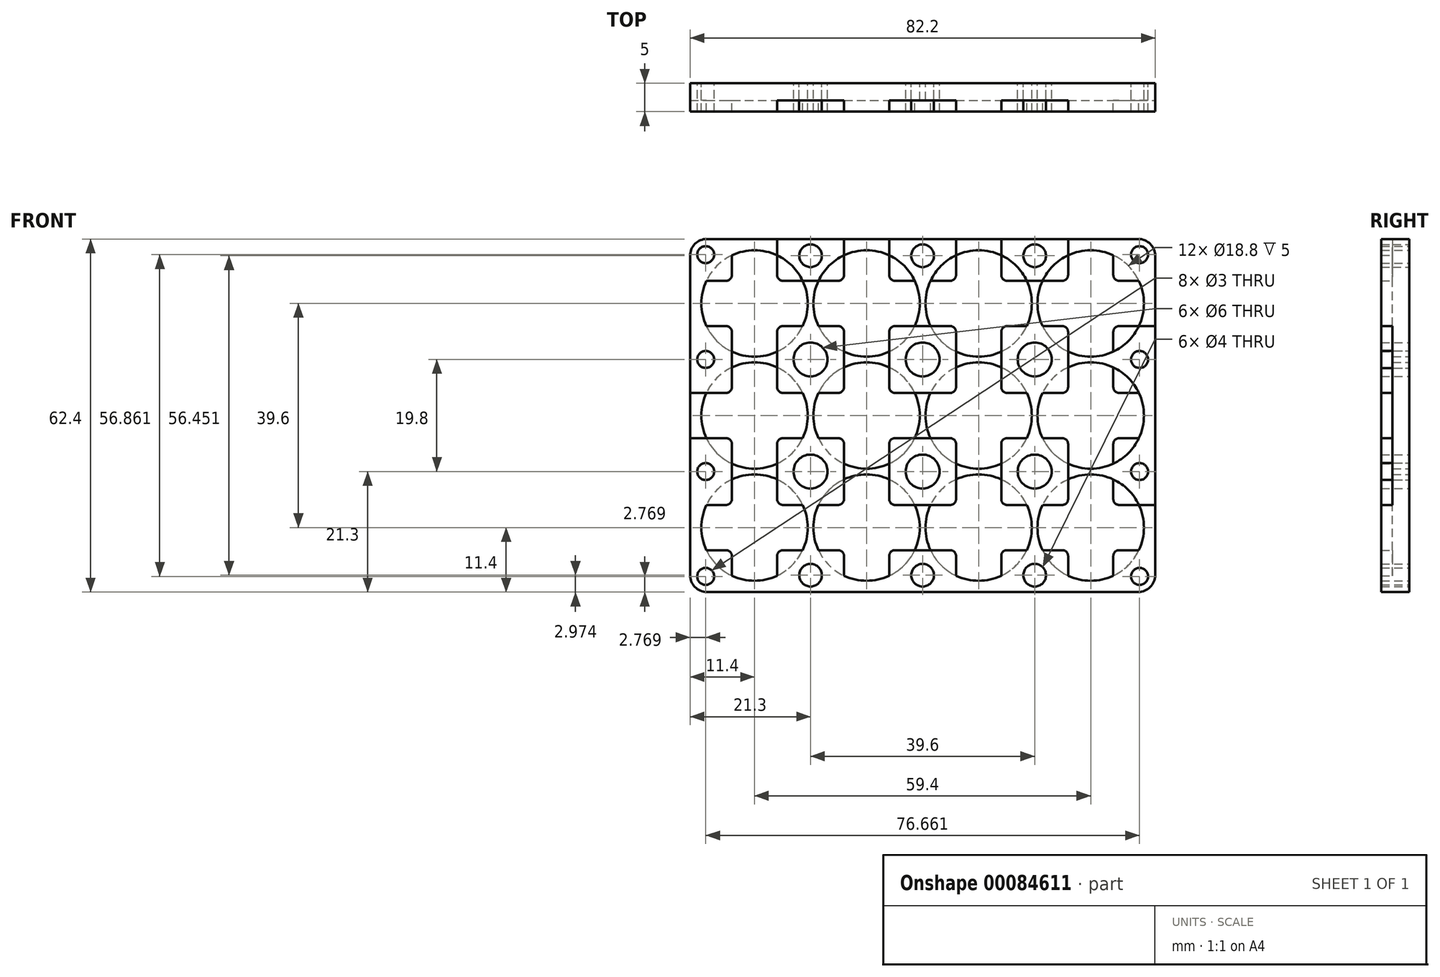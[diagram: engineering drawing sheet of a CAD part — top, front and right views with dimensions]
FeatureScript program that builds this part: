
annotation { "Feature Type Name" : "Feature", "Feature Type Description" : "" }
export const myFeature = defineFeature(function(context is Context, id is Id, definition is map)
    precondition{}
    {
        {
            var Q0;
            Q0=qCreatedBy(makeId("Front.planeOp"),FACE);
            var sketch = newSketch(context, id + "F0", { "sketchPlane" : qUnion([Q0]) });
            skCircle(sketch, "E0", {"center": v(0, 0) * mm, "radius": 9.4 * mm});
            skCircle(sketch, "E1.0.1.0", {"center": v(0, 19.8) * mm, "radius": 9.4 * mm});
            skCircle(sketch, "E1.0.2.0", {"center": v(0, 39.6) * mm, "radius": 9.4 * mm});
            skCircle(sketch, "E1.1.0.0", {"center": v(19.8, 0) * mm, "radius": 9.4 * mm});
            skCircle(sketch, "E1.1.1.0", {"center": v(19.8, 19.8) * mm, "radius": 9.4 * mm});
            skCircle(sketch, "E1.1.2.0", {"center": v(19.8, 39.6) * mm, "radius": 9.4 * mm});
            skCircle(sketch, "E1.2.0.0", {"center": v(39.6, 0) * mm, "radius": 9.4 * mm});
            skCircle(sketch, "E1.2.1.0", {"center": v(39.6, 19.8) * mm, "radius": 9.4 * mm});
            skCircle(sketch, "E1.2.2.0", {"center": v(39.6, 39.6) * mm, "radius": 9.4 * mm});
            skCircle(sketch, "E1.3.0.0", {"center": v(59.4, 0) * mm, "radius": 9.4 * mm});
            skCircle(sketch, "E1.3.1.0", {"center": v(59.4, 19.8) * mm, "radius": 9.4 * mm});
            skCircle(sketch, "E1.3.2.0", {"center": v(59.4, 39.6) * mm, "radius": 9.4 * mm});
            skLineSegment(sketch, "E1.direction1", {"start": v(0, 0) * mm, "end": v(19.8, 0) * mm, "construction": true});
            skLineSegment(sketch, "E1.direction2", {"start": v(0, 0) * mm, "end": v(0, 19.8) * mm, "construction": true});
            skLineSegment(sketch, "E2", {"start": v(-9.4, 19.8) * mm, "end": v(68.8, 19.8) * mm, "construction": true});
            skLineSegment(sketch, "E3", {"start": v(29.7, 19.8) * mm, "end": v(29.7, -16.3) * mm, "construction": true});
            skLineSegment(sketch, "E4.bottom", {"start": v(70.8, -11.4) * mm, "end": v(-11.4, -11.4) * mm});
            skLineSegment(sketch, "E4.top", {"start": v(70.8, 51) * mm, "end": v(-11.4, 51) * mm});
            skLineSegment(sketch, "E4.left", {"start": v(70.8, -11.4) * mm, "end": v(70.8, 51) * mm});
            skLineSegment(sketch, "E4.right", {"start": v(-11.4, -11.4) * mm, "end": v(-11.4, 51) * mm});
            skPoint(sketch, "E4.middle", {"position": v(29.7, 19.8) * mm});
            skLineSegment(sketch, "E5", {"start": v(19.8, 19.8) * mm, "end": v(0, 0) * mm, "construction": true});
            skLineSegment(sketch, "E6", {"start": v(19.8, 0) * mm, "end": v(0, 19.8) * mm, "construction": true});
            skCircle(sketch, "E7", {"center": v(9.9, 9.9) * mm, "radius": 3 * mm});
            skCircle(sketch, "E8.0.1.0", {"center": v(9.9, 29.7) * mm, "radius": 3 * mm});
            skCircle(sketch, "E8.1.0.0", {"center": v(29.7, 9.9) * mm, "radius": 3 * mm});
            skCircle(sketch, "E8.1.1.0", {"center": v(29.7, 29.7) * mm, "radius": 3 * mm});
            skCircle(sketch, "E8.2.0.0", {"center": v(49.5, 9.9) * mm, "radius": 3 * mm});
            skCircle(sketch, "E8.2.1.0", {"center": v(49.5, 29.7) * mm, "radius": 3 * mm});
            skLineSegment(sketch, "E8.direction1", {"start": v(9.9, 9.9) * mm, "end": v(29.7, 9.9) * mm, "construction": true});
            skLineSegment(sketch, "E8.direction2", {"start": v(9.9, 9.9) * mm, "end": v(9.9, 29.7) * mm, "construction": true});
            skLineSegment(sketch, "E9", {"start": v(9.9, 0) * mm, "end": v(9.9, -11.4) * mm, "construction": true});
            skCircle(sketch, "E10", {"center": v(9.9, -8.43) * mm, "radius": 2 * mm});
            skCircle(sketch, "E11.1.0.0", {"center": v(29.7, -8.43) * mm, "radius": 2 * mm});
            skCircle(sketch, "E11.2.0.0", {"center": v(49.5, -8.43) * mm, "radius": 2 * mm});
            skLineSegment(sketch, "E11.direction1", {"start": v(9.9, -8.43) * mm, "end": v(29.7, -8.43) * mm, "construction": true});
            skCircle(sketch, "E12.MirrorC", {"center": v(9.9, 48.03) * mm, "radius": 2 * mm});
            skCircle(sketch, "E13.MirrorC", {"center": v(29.7, 48.03) * mm, "radius": 2 * mm});
            skCircle(sketch, "E14.MirrorC", {"center": v(49.5, 48.03) * mm, "radius": 2 * mm});
            skLineSegment(sketch, "E15", {"start": v(0, 0) * mm, "end": v(-11.4, -11.4) * mm, "construction": true});
            skCircle(sketch, "E16", {"center": v(-8.63, -8.63) * mm, "radius": 1.5 * mm});
            skCircle(sketch, "E17", {"center": v(-8.63, 9.9) * mm, "radius": 1.5 * mm});
            skCircle(sketch, "E18", {"center": v(-8.63, 29.7) * mm, "radius": 1.5 * mm});
            skCircle(sketch, "E19.MirrorC", {"center": v(-8.63, 48.23) * mm, "radius": 1.5 * mm});
            skCircle(sketch, "E20.MirrorC", {"center": v(68.03, -8.63) * mm, "radius": 1.5 * mm});
            skCircle(sketch, "E21.MirrorC", {"center": v(68.03, 9.9) * mm, "radius": 1.5 * mm});
            skCircle(sketch, "E22.MirrorC", {"center": v(68.03, 29.7) * mm, "radius": 1.5 * mm});
            skCircle(sketch, "E23.MirrorC", {"center": v(68.03, 48.23) * mm, "radius": 1.5 * mm});
            skSolve(sketch);
        }
        {
            var Q0;
            Q0=qSketchRegion(id+"F0",true);
            extrude(context, id + "F1", {"entities" : qUnion([Q0]), "depth" : 3 * mm});
        }
        {
            var Q0;
            Q0=makeQuery(id+"F1.opExtrude","SWEPT_EDGE",EDGE,{"disambiguationData":[OSD([sQuery(id+"F0.wireOp",EDGE,"E4.top"),sQuery(id+"F0.wireOp",EDGE,"E4.left")])]});
            var Q1;
            Q1=makeQuery(id+"F1.opExtrude","SWEPT_EDGE",EDGE,{"disambiguationData":[OSD([sQuery(id+"F0.wireOp",EDGE,"E4.top"),sQuery(id+"F0.wireOp",EDGE,"E4.right")])]});
            var Q2;
            Q2=makeQuery(id+"F1.opExtrude","SWEPT_EDGE",EDGE,{"disambiguationData":[OSD([sQuery(id+"F0.wireOp",EDGE,"E4.bottom"),sQuery(id+"F0.wireOp",EDGE,"E4.right")])]});
            var Q3;
            Q3=makeQuery(id+"F1.opExtrude","SWEPT_EDGE",EDGE,{"disambiguationData":[OSD([sQuery(id+"F0.wireOp",EDGE,"E4.bottom"),sQuery(id+"F0.wireOp",EDGE,"E4.left")])]});
            fillet(context, id + "F2", {"entities" : qUnion([Q0, Q1, Q2, Q3]), "radius" : 3 * mm, "tangentPropagation" : true, "conicFillet" : false});
        }
        {
            var Q0;
            Q0=makeQuery(id+"F1.opExtrude","CAP_FACE",FACE,{"disambiguationData":[OSD([sQuery(id+"F0.wireOp",EDGE,"E0"),sQuery(id+"F0.wireOp",EDGE,"E1.0.1.0"),sQuery(id+"F0.wireOp",EDGE,"E1.0.2.0"),sQuery(id+"F0.wireOp",EDGE,"E1.1.0.0"),sQuery(id+"F0.wireOp",EDGE,"E1.1.1.0"),sQuery(id+"F0.wireOp",EDGE,"E1.1.2.0"),sQuery(id+"F0.wireOp",EDGE,"E1.2.0.0"),sQuery(id+"F0.wireOp",EDGE,"E1.2.1.0"),sQuery(id+"F0.wireOp",EDGE,"E1.2.2.0"),sQuery(id+"F0.wireOp",EDGE,"E1.3.0.0"),sQuery(id+"F0.wireOp",EDGE,"E1.3.1.0"),sQuery(id+"F0.wireOp",EDGE,"E1.3.2.0"),sQuery(id+"F0.wireOp",EDGE,"E4.bottom"),sQuery(id+"F0.wireOp",EDGE,"E4.top"),sQuery(id+"F0.wireOp",EDGE,"E4.left"),sQuery(id+"F0.wireOp",EDGE,"E4.right"),sQuery(id+"F0.wireOp",EDGE,"E7"),sQuery(id+"F0.wireOp",EDGE,"E8.0.1.0"),sQuery(id+"F0.wireOp",EDGE,"E8.1.0.0"),sQuery(id+"F0.wireOp",EDGE,"E8.1.1.0"),sQuery(id+"F0.wireOp",EDGE,"E8.2.0.0"),sQuery(id+"F0.wireOp",EDGE,"E8.2.1.0"),sQuery(id+"F0.wireOp",EDGE,"E10"),sQuery(id+"F0.wireOp",EDGE,"E11.1.0.0"),sQuery(id+"F0.wireOp",EDGE,"E11.2.0.0"),sQuery(id+"F0.wireOp",EDGE,"E12.MirrorC"),sQuery(id+"F0.wireOp",EDGE,"E13.MirrorC"),sQuery(id+"F0.wireOp",EDGE,"E14.MirrorC"),sQuery(id+"F0.wireOp",EDGE,"E16"),sQuery(id+"F0.wireOp",EDGE,"E17"),sQuery(id+"F0.wireOp",EDGE,"E18"),sQuery(id+"F0.wireOp",EDGE,"E19.MirrorC"),sQuery(id+"F0.wireOp",EDGE,"E20.MirrorC"),sQuery(id+"F0.wireOp",EDGE,"E21.MirrorC"),sQuery(id+"F0.wireOp",EDGE,"E22.MirrorC"),sQuery(id+"F0.wireOp",EDGE,"E23.MirrorC")])],"isStart":false});
            var sketch = newSketch(context, id + "F3", { "sketchPlane" : qUnion([Q0]) });
            skLineSegment(sketch, "E24.0", {"start": v(67.8, 51) * mm, "end": v(-8.4, 51) * mm});
            skArc(sketch, "E24.1", {"start": v(-8.4, 51) * mm, "mid": v(-10.52, 50.12) * mm, "end": v(-11.4, 48) * mm});
            skLineSegment(sketch, "E24.2", {"start": v(-11.4, -8.4) * mm, "end": v(-11.4, 35.6) * mm});
            skArc(sketch, "E24.3", {"start": v(-11.4, -8.4) * mm, "mid": v(-10.52, -10.52) * mm, "end": v(-8.4, -11.4) * mm});
            skLineSegment(sketch, "E24.4", {"start": v(67.8, -11.4) * mm, "end": v(-8.4, -11.4) * mm});
            skArc(sketch, "E24.5", {"start": v(67.8, -11.4) * mm, "mid": v(69.92, -10.52) * mm, "end": v(70.8, -8.4) * mm});
            skLineSegment(sketch, "E24.6", {"start": v(70.8, -8.4) * mm, "end": v(70.8, 48) * mm});
            skArc(sketch, "E24.7", {"start": v(70.8, 48) * mm, "mid": v(69.92, 50.12) * mm, "end": v(67.8, 51) * mm});
            skCircle(sketch, "E24.8", {"center": v(59.4, 39.6) * mm, "radius": 9.4 * mm});
            skCircle(sketch, "E24.9", {"center": v(39.6, 39.6) * mm, "radius": 9.4 * mm});
            skCircle(sketch, "E24.10", {"center": v(19.8, 39.6) * mm, "radius": 9.4 * mm});
            skArc(sketch, "E24.11", {"start": v(-8.5, 43.6) * mm, "mid": v(-9.4, 39.6) * mm, "end": v(-8.5, 35.6) * mm});
            skCircle(sketch, "E24.12", {"center": v(0, 19.8) * mm, "radius": 9.4 * mm});
            skCircle(sketch, "E24.13", {"center": v(19.8, 19.8) * mm, "radius": 9.4 * mm});
            skCircle(sketch, "E24.14", {"center": v(39.6, 19.8) * mm, "radius": 9.4 * mm});
            skCircle(sketch, "E24.15", {"center": v(59.4, 19.8) * mm, "radius": 9.4 * mm});
            skCircle(sketch, "E24.16", {"center": v(59.4, 0) * mm, "radius": 9.4 * mm});
            skCircle(sketch, "E24.17", {"center": v(39.6, 0) * mm, "radius": 9.4 * mm});
            skCircle(sketch, "E24.18", {"center": v(19.8, 0) * mm, "radius": 9.4 * mm});
            skCircle(sketch, "E24.19", {"center": v(0, 0) * mm, "radius": 9.4 * mm});
            skLineSegment(sketch, "E25.left", {"start": v(-11.4, 39.6) * mm, "end": v(-11.4, 43.6) * mm});
            skLineSegment(sketch, "E25.right", {"start": v(70.8, 39.6) * mm, "end": v(70.8, 43.6) * mm});
            skLineSegment(sketch, "E26.trimOffspring", {"start": v(-11.4, 43.6) * mm, "end": v(-11.4, 48) * mm});
            skLineSegment(sketch, "E27", {"start": v(-4, 51) * mm, "end": v(-4, 43.6) * mm});
            skLineSegment(sketch, "E28.MirrorCS", {"start": v(4, 51) * mm, "end": v(4, 43.6) * mm});
            skLineSegment(sketch, "E29", {"start": v(-11.4, -4) * mm, "end": v(-4, -4) * mm});
            skLineSegment(sketch, "E30.MirrorCS", {"start": v(-11.4, 4) * mm, "end": v(-4, 4) * mm});
            skLineSegment(sketch, "E31.1.0.0", {"start": v(15.8, 51) * mm, "end": v(15.8, 43.6) * mm});
            skLineSegment(sketch, "E31.1.0.1", {"start": v(23.8, 51) * mm, "end": v(23.8, 43.6) * mm});
            skLineSegment(sketch, "E31.2.0.0", {"start": v(35.6, 51) * mm, "end": v(35.6, 43.6) * mm});
            skLineSegment(sketch, "E31.2.0.1", {"start": v(43.6, 51) * mm, "end": v(43.6, 43.6) * mm});
            skLineSegment(sketch, "E31.3.0.0", {"start": v(55.4, 51) * mm, "end": v(55.4, 43.6) * mm});
            skLineSegment(sketch, "E31.3.0.1", {"start": v(63.4, 51) * mm, "end": v(63.4, 43.6) * mm});
            skLineSegment(sketch, "E31.direction1", {"start": v(-4, -11.4) * mm, "end": v(15.8, -11.4) * mm, "construction": true});
            skLineSegment(sketch, "E32.0.1.0", {"start": v(-11.4, 23.8) * mm, "end": v(-4, 23.8) * mm});
            skLineSegment(sketch, "E32.0.1.1", {"start": v(-11.4, 15.8) * mm, "end": v(-4, 15.8) * mm});
            skLineSegment(sketch, "E32.0.2.0", {"start": v(-11.4, 43.6) * mm, "end": v(-4, 43.6) * mm});
            skLineSegment(sketch, "E32.0.2.1", {"start": v(-11.4, 35.6) * mm, "end": v(-4, 35.6) * mm});
            skLineSegment(sketch, "E32.direction1", {"start": v(-11.4, 4) * mm, "end": v(-4, 4) * mm, "construction": true});
            skLineSegment(sketch, "E32.direction2", {"start": v(-11.4, 4) * mm, "end": v(-11.4, 23.8) * mm, "construction": true});
            skLineSegment(sketch, "E33.trimOffspring", {"start": v(4, 35.6) * mm, "end": v(15.8, 35.6) * mm});
            skLineSegment(sketch, "E34.trimOffspring", {"start": v(4, 43.6) * mm, "end": v(15.8, 43.6) * mm});
            skLineSegment(sketch, "E35.trimOffspring", {"start": v(4, 35.6) * mm, "end": v(4, 23.8) * mm});
            skLineSegment(sketch, "E36.trimOffspring", {"start": v(-4, 35.6) * mm, "end": v(-4, 23.8) * mm});
            skLineSegment(sketch, "E37.trimOffspring", {"start": v(15.8, 35.6) * mm, "end": v(15.8, 23.8) * mm});
            skLineSegment(sketch, "E38.trimOffspring", {"start": v(23.8, 35.6) * mm, "end": v(23.8, 23.8) * mm});
            skLineSegment(sketch, "E39.trimOffspring", {"start": v(35.6, 35.6) * mm, "end": v(35.6, 23.8) * mm});
            skLineSegment(sketch, "E40.trimOffspring", {"start": v(43.6, 35.6) * mm, "end": v(43.6, 23.8) * mm});
            skLineSegment(sketch, "E41.trimOffspring", {"start": v(55.4, 35.6) * mm, "end": v(55.4, 23.8) * mm});
            skLineSegment(sketch, "E42.trimOffspring", {"start": v(63.4, 35.6) * mm, "end": v(63.4, 23.8) * mm});
            skLineSegment(sketch, "E43.trimOffspring", {"start": v(23.8, 43.6) * mm, "end": v(35.6, 43.6) * mm});
            skLineSegment(sketch, "E44.trimOffspring", {"start": v(43.6, 43.6) * mm, "end": v(55.4, 43.6) * mm});
            skLineSegment(sketch, "E45.trimOffspring", {"start": v(63.4, 43.6) * mm, "end": v(70.8, 43.6) * mm});
            skLineSegment(sketch, "E46.trimOffspring", {"start": v(63.4, 35.6) * mm, "end": v(70.8, 35.6) * mm});
            skLineSegment(sketch, "E47.trimOffspring", {"start": v(43.6, 35.6) * mm, "end": v(55.4, 35.6) * mm});
            skLineSegment(sketch, "E48.trimOffspring", {"start": v(23.8, 35.6) * mm, "end": v(35.6, 35.6) * mm});
            skLineSegment(sketch, "E49.trimOffspring", {"start": v(4, 23.8) * mm, "end": v(15.8, 23.8) * mm});
            skLineSegment(sketch, "E50.trimOffspring", {"start": v(4, 15.8) * mm, "end": v(11.3, 15.8) * mm});
            skLineSegment(sketch, "E51.trimOffspring", {"start": v(-4, 15.8) * mm, "end": v(-4, 4) * mm});
            skLineSegment(sketch, "E52.trimOffspring", {"start": v(4, 15.8) * mm, "end": v(4, 4) * mm});
            skLineSegment(sketch, "E53.trimOffspring", {"start": v(15.8, 15.8) * mm, "end": v(15.8, 4) * mm});
            skLineSegment(sketch, "E54.trimOffspring", {"start": v(23.8, 15.8) * mm, "end": v(23.8, 4) * mm});
            skLineSegment(sketch, "E55.trimOffspring", {"start": v(35.6, 15.8) * mm, "end": v(35.6, 4) * mm});
            skLineSegment(sketch, "E56.trimOffspring", {"start": v(43.6, 15.8) * mm, "end": v(43.6, 4) * mm});
            skLineSegment(sketch, "E57.trimOffspring", {"start": v(55.4, 15.8) * mm, "end": v(55.4, 4) * mm});
            skLineSegment(sketch, "E58.trimOffspring", {"start": v(63.4, 15.8) * mm, "end": v(63.4, 4) * mm});
            skLineSegment(sketch, "E59.trimOffspring", {"start": v(23.8, 23.8) * mm, "end": v(35.6, 23.8) * mm});
            skLineSegment(sketch, "E60.trimOffspring", {"start": v(43.6, 23.8) * mm, "end": v(55.4, 23.8) * mm});
            skLineSegment(sketch, "E61.trimOffspring", {"start": v(63.4, 23.8) * mm, "end": v(70.8, 23.8) * mm});
            skLineSegment(sketch, "E62.trimOffspring", {"start": v(23.8, 15.8) * mm, "end": v(35.6, 15.8) * mm});
            skLineSegment(sketch, "E63.trimOffspring", {"start": v(63.4, 15.8) * mm, "end": v(70.8, 15.8) * mm});
            skLineSegment(sketch, "E64.trimOffspring", {"start": v(63.4, 4) * mm, "end": v(70.8, 4) * mm});
            skLineSegment(sketch, "E65.trimOffspring", {"start": v(43.6, 4) * mm, "end": v(55.4, 4) * mm});
            skLineSegment(sketch, "E66.trimOffspring", {"start": v(23.8, 4) * mm, "end": v(35.6, 4) * mm});
            skLineSegment(sketch, "E67.trimOffspring", {"start": v(4, 4) * mm, "end": v(15.8, 4) * mm});
            skLineSegment(sketch, "E68.trimOffspring", {"start": v(4, -4) * mm, "end": v(11.3, -4) * mm});
            skLineSegment(sketch, "E69.trimOffspring", {"start": v(23.8, -4) * mm, "end": v(35.6, -4) * mm});
            skLineSegment(sketch, "E70.trimOffspring", {"start": v(63.4, -4) * mm, "end": v(70.8, -4) * mm});
            skLineSegment(sketch, "E71.trimOffspring", {"start": v(55.4, -4) * mm, "end": v(55.4, -11.4) * mm});
            skLineSegment(sketch, "E72.trimOffspring", {"start": v(63.4, -4) * mm, "end": v(63.4, -11.4) * mm});
            skLineSegment(sketch, "E73.trimOffspring", {"start": v(43.6, -4) * mm, "end": v(43.6, -11.4) * mm});
            skLineSegment(sketch, "E74.trimOffspring", {"start": v(35.6, -4) * mm, "end": v(35.6, -11.4) * mm});
            skLineSegment(sketch, "E75.trimOffspring", {"start": v(23.8, -4) * mm, "end": v(23.8, -11.4) * mm});
            skLineSegment(sketch, "E76.trimOffspring", {"start": v(4, -4) * mm, "end": v(4, -11.4) * mm});
            skLineSegment(sketch, "E77.trimOffspring", {"start": v(-4, -4) * mm, "end": v(-4, -11.4) * mm});
            skLineSegment(sketch, "E78", {"start": v(11.3, 15.8) * mm, "end": v(15.8, 15.8) * mm});
            skLineSegment(sketch, "E79", {"start": v(11.3, -4) * mm, "end": v(15.8, -4) * mm});
            skLineSegment(sketch, "E80.trimOffspring", {"start": v(15.8, -4) * mm, "end": v(15.8, -11.4) * mm});
            skLineSegment(sketch, "E81.trimOffspring", {"start": v(43.6, 15.8) * mm, "end": v(55.4, 15.8) * mm});
            skLineSegment(sketch, "E82.trimOffspring", {"start": v(4, 4) * mm, "end": v(13.6, 4) * mm, "construction": true});
            skLineSegment(sketch, "E83.trimOffspring", {"start": v(43.6, -4) * mm, "end": v(55.4, -4) * mm});
            skArc(sketch, "E84.trimOffspring", {"start": v(4, 48.1) * mm, "mid": v(0, 49) * mm, "end": v(-4, 48.1) * mm});
            skArc(sketch, "E85.trimOffspring", {"start": v(8.5, 35.6) * mm, "mid": v(9.4, 39.6) * mm, "end": v(8.5, 43.6) * mm});
            skArc(sketch, "E86.trimOffspring", {"start": v(-4, 31.1) * mm, "mid": v(0, 30.2) * mm, "end": v(4, 31.1) * mm});
            skSolve(sketch);
        }
        {
            var Q0;
            {var subQ6=sQuery(id+"F3.wireOp",EDGE,"E24.1");Q0=makeQuery(id+"F3.imprint","IMPRINT",FACE,{"disambiguationData":[TD([[makeQuery(id+"F3.imprint","IMPRINT",EDGE,{"derivedFrom":subQ6}),1.0]])]});}
            var Q1;
            {var subQ0=sQuery(id+"F3.wireOp",EDGE,"E32.0.2.0");var subQ1=sQuery(id+"F3.wireOp",EDGE,"E27");var subQ2=makeQuery(id+"F3.imprint","INTERSECT",VERTEX,{"derivedFrom":[subQ1,subQ0]});Q1=makeQuery(id+"F3.imprint","IMPRINT",FACE,{"disambiguationData":[TD([[makeQuery(id+"F3.imprint","IMPRINT",EDGE,{"disambiguationData":[TD([[subQ2,1.0]])],"derivedFrom":subQ1}),-1.0]])]});}
            var Q2;
            {var subQ0=sQuery(id+"F3.wireOp",EDGE,"E34.trimOffspring");var subQ1=sQuery(id+"F3.wireOp",EDGE,"E28.MirrorCS");var subQ2=makeQuery(id+"F3.imprint","INTERSECT",VERTEX,{"derivedFrom":[subQ1,subQ0]});Q2=makeQuery(id+"F3.imprint","IMPRINT",FACE,{"disambiguationData":[TD([[makeQuery(id+"F3.imprint","IMPRINT",EDGE,{"disambiguationData":[TD([[subQ2,1.0]])],"derivedFrom":subQ1}),1.0]])]});}
            var Q3;
            Q3=makeQuery(id+"F3.imprint","IMPRINT",FACE,{"disambiguationData":[TD([[makeQuery(id+"F3.imprint","IMPRINT",EDGE,{"derivedFrom":makeQuery(id+"F1.opExtrude","CAP_EDGE",EDGE,{"disambiguationData":[OSD([sQuery(id+"F0.wireOp",EDGE,"E12.MirrorC")])],"isStart":false})}),1.0]])]});
            var Q4;
            {var subQ0=sQuery(id+"F3.wireOp",EDGE,"E34.trimOffspring");var subQ1=sQuery(id+"F3.wireOp",EDGE,"E31.1.0.0");var subQ2=makeQuery(id+"F3.imprint","INTERSECT",VERTEX,{"derivedFrom":[subQ1,subQ0]});Q4=makeQuery(id+"F3.imprint","IMPRINT",FACE,{"disambiguationData":[TD([[makeQuery(id+"F3.imprint","IMPRINT",EDGE,{"disambiguationData":[TD([[subQ2,1.0]])],"derivedFrom":subQ1}),-1.0]])]});}
            var Q5;
            {var subQ0=sQuery(id+"F3.wireOp",EDGE,"E43.trimOffspring");var subQ1=sQuery(id+"F3.wireOp",EDGE,"E31.1.0.1");var subQ2=makeQuery(id+"F3.imprint","INTERSECT",VERTEX,{"derivedFrom":[subQ1,subQ0]});Q5=makeQuery(id+"F3.imprint","IMPRINT",FACE,{"disambiguationData":[TD([[makeQuery(id+"F3.imprint","IMPRINT",EDGE,{"disambiguationData":[TD([[subQ2,1.0]])],"derivedFrom":subQ1}),1.0]])]});}
            var Q6;
            Q6=makeQuery(id+"F3.imprint","IMPRINT",FACE,{"disambiguationData":[TD([[makeQuery(id+"F3.imprint","IMPRINT",EDGE,{"derivedFrom":makeQuery(id+"F1.opExtrude","CAP_EDGE",EDGE,{"disambiguationData":[OSD([sQuery(id+"F0.wireOp",EDGE,"E13.MirrorC")])],"isStart":false})}),1.0]])]});
            var Q7;
            {var subQ0=sQuery(id+"F3.wireOp",EDGE,"E31.2.0.0");var subQ1=sQuery(id+"F3.wireOp",EDGE,"E24.9");var subQ2=makeQuery(id+"F3.imprint","INTERSECT",VERTEX,{"derivedFrom":[subQ1,subQ0]});Q7=makeQuery(id+"F3.imprint","IMPRINT",FACE,{"disambiguationData":[TD([[makeQuery(id+"F3.imprint","IMPRINT",EDGE,{"disambiguationData":[TD([[subQ2,-1.0]])],"derivedFrom":subQ1}),1.0]])]});}
            var Q8;
            {var subQ0=sQuery(id+"F3.wireOp",EDGE,"E31.2.0.1");var subQ1=sQuery(id+"F3.wireOp",EDGE,"E24.9");var subQ2=makeQuery(id+"F3.imprint","INTERSECT",VERTEX,{"derivedFrom":[subQ1,subQ0]});Q8=makeQuery(id+"F3.imprint","IMPRINT",FACE,{"disambiguationData":[TD([[makeQuery(id+"F3.imprint","IMPRINT",EDGE,{"disambiguationData":[TD([[subQ2,1.0]])],"derivedFrom":subQ1}),1.0]])]});}
            var Q9;
            Q9=makeQuery(id+"F3.imprint","IMPRINT",FACE,{"disambiguationData":[TD([[makeQuery(id+"F3.imprint","IMPRINT",EDGE,{"derivedFrom":makeQuery(id+"F1.opExtrude","CAP_EDGE",EDGE,{"disambiguationData":[OSD([sQuery(id+"F0.wireOp",EDGE,"E14.MirrorC")])],"isStart":false})}),1.0]])]});
            var Q10;
            {var subQ0=sQuery(id+"F3.wireOp",EDGE,"E44.trimOffspring");var subQ1=sQuery(id+"F3.wireOp",EDGE,"E31.3.0.0");var subQ2=makeQuery(id+"F3.imprint","INTERSECT",VERTEX,{"derivedFrom":[subQ1,subQ0]});Q10=makeQuery(id+"F3.imprint","IMPRINT",FACE,{"disambiguationData":[TD([[makeQuery(id+"F3.imprint","IMPRINT",EDGE,{"disambiguationData":[TD([[subQ2,1.0]])],"derivedFrom":subQ1}),-1.0]])]});}
            var Q11;
            {var subQ0=sQuery(id+"F3.wireOp",EDGE,"E45.trimOffspring");var subQ1=sQuery(id+"F3.wireOp",EDGE,"E31.3.0.1");var subQ2=makeQuery(id+"F3.imprint","INTERSECT",VERTEX,{"derivedFrom":[subQ1,subQ0]});Q11=makeQuery(id+"F3.imprint","IMPRINT",FACE,{"disambiguationData":[TD([[makeQuery(id+"F3.imprint","IMPRINT",EDGE,{"disambiguationData":[TD([[subQ2,1.0]])],"derivedFrom":subQ1}),1.0]])]});}
            var Q12;
            {var subQ9=sQuery(id+"F3.wireOp",EDGE,"E24.7");Q12=makeQuery(id+"F3.imprint","IMPRINT",FACE,{"disambiguationData":[TD([[makeQuery(id+"F3.imprint","IMPRINT",EDGE,{"derivedFrom":subQ9}),1.0]])]});}
            var Q13;
            {var subQ0=sQuery(id+"F3.wireOp",EDGE,"E61.trimOffspring");var subQ1=sQuery(id+"F3.wireOp",EDGE,"E42.trimOffspring");var subQ2=makeQuery(id+"F3.imprint","INTERSECT",VERTEX,{"derivedFrom":[subQ1,subQ0]});Q13=makeQuery(id+"F3.imprint","IMPRINT",FACE,{"disambiguationData":[TD([[makeQuery(id+"F3.imprint","IMPRINT",EDGE,{"disambiguationData":[TD([[subQ2,1.0]])],"derivedFrom":subQ1}),1.0]])]});}
            var Q14;
            Q14=makeQuery(id+"F3.imprint","IMPRINT",FACE,{"disambiguationData":[TD([[makeQuery(id+"F3.imprint","IMPRINT",EDGE,{"derivedFrom":makeQuery(id+"F1.opExtrude","CAP_EDGE",EDGE,{"disambiguationData":[OSD([sQuery(id+"F0.wireOp",EDGE,"E22.MirrorC")])],"isStart":false})}),1.0]])]});
            var Q15;
            {var subQ0=sQuery(id+"F3.wireOp",EDGE,"E46.trimOffspring");var subQ1=sQuery(id+"F3.wireOp",EDGE,"E42.trimOffspring");var subQ2=makeQuery(id+"F3.imprint","INTERSECT",VERTEX,{"derivedFrom":[subQ1,subQ0]});Q15=makeQuery(id+"F3.imprint","IMPRINT",FACE,{"disambiguationData":[TD([[makeQuery(id+"F3.imprint","IMPRINT",EDGE,{"disambiguationData":[TD([[subQ2,-1.0]])],"derivedFrom":subQ1}),1.0]])]});}
            var Q16;
            {var subQ0=sQuery(id+"F3.wireOp",EDGE,"E60.trimOffspring");var subQ1=sQuery(id+"F3.wireOp",EDGE,"E41.trimOffspring");var subQ2=makeQuery(id+"F3.imprint","INTERSECT",VERTEX,{"derivedFrom":[subQ1,subQ0]});Q16=makeQuery(id+"F3.imprint","IMPRINT",FACE,{"disambiguationData":[TD([[makeQuery(id+"F3.imprint","IMPRINT",EDGE,{"disambiguationData":[TD([[subQ2,1.0]])],"derivedFrom":subQ1}),-1.0]])]});}
            var Q17;
            {var subQ0=sQuery(id+"F3.wireOp",EDGE,"E60.trimOffspring");var subQ1=sQuery(id+"F3.wireOp",EDGE,"E40.trimOffspring");var subQ2=makeQuery(id+"F3.imprint","INTERSECT",VERTEX,{"derivedFrom":[subQ1,subQ0]});Q17=makeQuery(id+"F3.imprint","IMPRINT",FACE,{"disambiguationData":[TD([[makeQuery(id+"F3.imprint","IMPRINT",EDGE,{"disambiguationData":[TD([[subQ2,1.0]])],"derivedFrom":subQ1}),1.0]])]});}
            var Q18;
            {var subQ0=sQuery(id+"F3.wireOp",EDGE,"E40.trimOffspring");var subQ1=sQuery(id+"F3.wireOp",EDGE,"E24.9");var subQ2=makeQuery(id+"F3.imprint","INTERSECT",VERTEX,{"derivedFrom":[subQ1,subQ0]});Q18=makeQuery(id+"F3.imprint","IMPRINT",FACE,{"disambiguationData":[TD([[makeQuery(id+"F3.imprint","IMPRINT",EDGE,{"disambiguationData":[TD([[subQ2,-1.0]])],"derivedFrom":subQ1}),1.0]])]});}
            var Q19;
            {var subQ0=sQuery(id+"F3.wireOp",EDGE,"E47.trimOffspring");var subQ1=sQuery(id+"F3.wireOp",EDGE,"E41.trimOffspring");var subQ2=makeQuery(id+"F3.imprint","INTERSECT",VERTEX,{"derivedFrom":[subQ1,subQ0]});Q19=makeQuery(id+"F3.imprint","IMPRINT",FACE,{"disambiguationData":[TD([[makeQuery(id+"F3.imprint","IMPRINT",EDGE,{"disambiguationData":[TD([[subQ2,-1.0]])],"derivedFrom":subQ1}),-1.0]])]});}
            var Q20;
            Q20=makeQuery(id+"F3.imprint","IMPRINT",FACE,{"disambiguationData":[TD([[makeQuery(id+"F3.imprint","IMPRINT",EDGE,{"derivedFrom":makeQuery(id+"F1.opExtrude","CAP_EDGE",EDGE,{"disambiguationData":[OSD([sQuery(id+"F0.wireOp",EDGE,"E8.2.1.0")])],"isStart":false})}),-1.0]])]});
            var Q21;
            {var subQ0=sQuery(id+"F3.wireOp",EDGE,"E48.trimOffspring");var subQ1=sQuery(id+"F3.wireOp",EDGE,"E38.trimOffspring");var subQ2=makeQuery(id+"F3.imprint","INTERSECT",VERTEX,{"derivedFrom":[subQ1,subQ0]});Q21=makeQuery(id+"F3.imprint","IMPRINT",FACE,{"disambiguationData":[TD([[makeQuery(id+"F3.imprint","IMPRINT",EDGE,{"disambiguationData":[TD([[subQ2,-1.0]])],"derivedFrom":subQ1}),1.0]])]});}
            var Q22;
            {var subQ0=sQuery(id+"F3.wireOp",EDGE,"E59.trimOffspring");var subQ1=sQuery(id+"F3.wireOp",EDGE,"E38.trimOffspring");var subQ2=makeQuery(id+"F3.imprint","INTERSECT",VERTEX,{"derivedFrom":[subQ1,subQ0]});Q22=makeQuery(id+"F3.imprint","IMPRINT",FACE,{"disambiguationData":[TD([[makeQuery(id+"F3.imprint","IMPRINT",EDGE,{"disambiguationData":[TD([[subQ2,1.0]])],"derivedFrom":subQ1}),1.0]])]});}
            var Q23;
            {var subQ0=sQuery(id+"F3.wireOp",EDGE,"E59.trimOffspring");var subQ1=sQuery(id+"F3.wireOp",EDGE,"E39.trimOffspring");var subQ2=makeQuery(id+"F3.imprint","INTERSECT",VERTEX,{"derivedFrom":[subQ1,subQ0]});Q23=makeQuery(id+"F3.imprint","IMPRINT",FACE,{"disambiguationData":[TD([[makeQuery(id+"F3.imprint","IMPRINT",EDGE,{"disambiguationData":[TD([[subQ2,1.0]])],"derivedFrom":subQ1}),-1.0]])]});}
            var Q24;
            {var subQ0=sQuery(id+"F3.wireOp",EDGE,"E48.trimOffspring");var subQ1=sQuery(id+"F3.wireOp",EDGE,"E24.9");var subQ2=makeQuery(id+"F3.imprint","INTERSECT",VERTEX,{"derivedFrom":[subQ1,subQ0]});Q24=makeQuery(id+"F3.imprint","IMPRINT",FACE,{"disambiguationData":[TD([[makeQuery(id+"F3.imprint","IMPRINT",EDGE,{"disambiguationData":[TD([[subQ2,-1.0]])],"derivedFrom":subQ1}),1.0]])]});}
            var Q25;
            Q25=makeQuery(id+"F3.imprint","IMPRINT",FACE,{"disambiguationData":[TD([[makeQuery(id+"F3.imprint","IMPRINT",EDGE,{"derivedFrom":makeQuery(id+"F1.opExtrude","CAP_EDGE",EDGE,{"disambiguationData":[OSD([sQuery(id+"F0.wireOp",EDGE,"E8.1.1.0")])],"isStart":false})}),-1.0]])]});
            var Q26;
            Q26=makeQuery(id+"F3.imprint","IMPRINT",FACE,{"disambiguationData":[TD([[makeQuery(id+"F3.imprint","IMPRINT",EDGE,{"derivedFrom":makeQuery(id+"F1.opExtrude","CAP_EDGE",EDGE,{"disambiguationData":[OSD([sQuery(id+"F0.wireOp",EDGE,"E8.0.1.0")])],"isStart":false})}),-1.0]])]});
            var Q27;
            {var subQ0=sQuery(id+"F3.wireOp",EDGE,"E35.trimOffspring");var subQ1=sQuery(id+"F3.wireOp",EDGE,"E33.trimOffspring");var subQ2=makeQuery(id+"F3.imprint","INTERSECT",VERTEX,{"derivedFrom":[subQ1,subQ0]});Q27=makeQuery(id+"F3.imprint","IMPRINT",FACE,{"disambiguationData":[TD([[makeQuery(id+"F3.imprint","IMPRINT",EDGE,{"disambiguationData":[TD([[subQ2,-1.0]])],"derivedFrom":subQ1}),-1.0]])]});}
            var Q28;
            {var subQ0=sQuery(id+"F3.wireOp",EDGE,"E37.trimOffspring");var subQ1=sQuery(id+"F3.wireOp",EDGE,"E33.trimOffspring");var subQ2=makeQuery(id+"F3.imprint","INTERSECT",VERTEX,{"derivedFrom":[subQ1,subQ0]});Q28=makeQuery(id+"F3.imprint","IMPRINT",FACE,{"disambiguationData":[TD([[makeQuery(id+"F3.imprint","IMPRINT",EDGE,{"disambiguationData":[TD([[subQ2,1.0]])],"derivedFrom":subQ1}),-1.0]])]});}
            var Q29;
            {var subQ0=sQuery(id+"F3.wireOp",EDGE,"E49.trimOffspring");var subQ1=sQuery(id+"F3.wireOp",EDGE,"E37.trimOffspring");var subQ2=makeQuery(id+"F3.imprint","INTERSECT",VERTEX,{"derivedFrom":[subQ1,subQ0]});Q29=makeQuery(id+"F3.imprint","IMPRINT",FACE,{"disambiguationData":[TD([[makeQuery(id+"F3.imprint","IMPRINT",EDGE,{"disambiguationData":[TD([[subQ2,1.0]])],"derivedFrom":subQ1}),-1.0]])]});}
            var Q30;
            {var subQ0=sQuery(id+"F3.wireOp",EDGE,"E49.trimOffspring");var subQ1=sQuery(id+"F3.wireOp",EDGE,"E35.trimOffspring");var subQ2=makeQuery(id+"F3.imprint","INTERSECT",VERTEX,{"derivedFrom":[subQ1,subQ0]});Q30=makeQuery(id+"F3.imprint","IMPRINT",FACE,{"disambiguationData":[TD([[makeQuery(id+"F3.imprint","IMPRINT",EDGE,{"disambiguationData":[TD([[subQ2,1.0]])],"derivedFrom":subQ1}),1.0]])]});}
            var Q31;
            Q31=makeQuery(id+"F3.imprint","IMPRINT",FACE,{"disambiguationData":[TD([[makeQuery(id+"F3.imprint","IMPRINT",EDGE,{"derivedFrom":makeQuery(id+"F1.opExtrude","CAP_EDGE",EDGE,{"disambiguationData":[OSD([sQuery(id+"F0.wireOp",EDGE,"E17")])],"isStart":false})}),-1.0]])]});
            var Q32;
            {var subQ0=sQuery(id+"F3.wireOp",EDGE,"E51.trimOffspring");var subQ1=sQuery(id+"F3.wireOp",EDGE,"E32.0.1.1");var subQ2=makeQuery(id+"F3.imprint","INTERSECT",VERTEX,{"derivedFrom":[subQ1,subQ0]});Q32=makeQuery(id+"F3.imprint","IMPRINT",FACE,{"disambiguationData":[TD([[makeQuery(id+"F3.imprint","IMPRINT",EDGE,{"disambiguationData":[TD([[subQ2,1.0]])],"derivedFrom":subQ1}),-1.0]])]});}
            var Q33;
            {var subQ0=sQuery(id+"F3.wireOp",EDGE,"E51.trimOffspring");var subQ1=sQuery(id+"F3.wireOp",EDGE,"E30.MirrorCS");var subQ2=makeQuery(id+"F3.imprint","INTERSECT",VERTEX,{"derivedFrom":[subQ1,subQ0]});Q33=makeQuery(id+"F3.imprint","IMPRINT",FACE,{"disambiguationData":[TD([[makeQuery(id+"F3.imprint","IMPRINT",EDGE,{"disambiguationData":[TD([[subQ2,1.0]])],"derivedFrom":subQ1}),1.0]])]});}
            var Q34;
            {var subQ1=sQuery(id+"F3.wireOp",EDGE,"E24.3");Q34=makeQuery(id+"F3.imprint","IMPRINT",FACE,{"disambiguationData":[TD([[makeQuery(id+"F3.imprint","IMPRINT",EDGE,{"derivedFrom":subQ1}),1.0]])]});}
            var Q35;
            {var subQ0=sQuery(id+"F3.wireOp",EDGE,"E77.trimOffspring");var subQ1=sQuery(id+"F3.wireOp",EDGE,"E29");var subQ2=makeQuery(id+"F3.imprint","INTERSECT",VERTEX,{"derivedFrom":[subQ1,subQ0]});Q35=makeQuery(id+"F3.imprint","IMPRINT",FACE,{"disambiguationData":[TD([[makeQuery(id+"F3.imprint","IMPRINT",EDGE,{"disambiguationData":[TD([[subQ2,1.0]])],"derivedFrom":subQ1}),-1.0]])]});}
            var Q36;
            Q36=makeQuery(id+"F3.imprint","IMPRINT",FACE,{"disambiguationData":[TD([[makeQuery(id+"F3.imprint","IMPRINT",EDGE,{"derivedFrom":makeQuery(id+"F1.opExtrude","CAP_EDGE",EDGE,{"disambiguationData":[OSD([sQuery(id+"F0.wireOp",EDGE,"E10")])],"isStart":false})}),-1.0]])]});
            var Q37;
            {var subQ0=sQuery(id+"F3.wireOp",EDGE,"E76.trimOffspring");var subQ1=sQuery(id+"F3.wireOp",EDGE,"E68.trimOffspring");var subQ2=makeQuery(id+"F3.imprint","INTERSECT",VERTEX,{"derivedFrom":[subQ1,subQ0]});Q37=makeQuery(id+"F3.imprint","IMPRINT",FACE,{"disambiguationData":[TD([[makeQuery(id+"F3.imprint","IMPRINT",EDGE,{"disambiguationData":[TD([[subQ2,-1.0]])],"derivedFrom":subQ1}),-1.0]])]});}
            var Q38;
            {var subQ0=sQuery(id+"F3.wireOp",EDGE,"E79");Q38=makeQuery(id+"F3.imprint","IMPRINT",FACE,{"disambiguationData":[TD([[makeQuery(id+"F3.imprint","IMPRINT",EDGE,{"derivedFrom":subQ0}),-1.0]])]});}
            var Q39;
            Q39=makeQuery(id+"F3.imprint","IMPRINT",FACE,{"disambiguationData":[TD([[makeQuery(id+"F3.imprint","IMPRINT",EDGE,{"derivedFrom":makeQuery(id+"F1.opExtrude","CAP_EDGE",EDGE,{"disambiguationData":[OSD([sQuery(id+"F0.wireOp",EDGE,"E11.1.0.0")])],"isStart":false})}),-1.0]])]});
            var Q40;
            {var subQ0=sQuery(id+"F3.wireOp",EDGE,"E75.trimOffspring");var subQ1=sQuery(id+"F3.wireOp",EDGE,"E69.trimOffspring");var subQ2=makeQuery(id+"F3.imprint","INTERSECT",VERTEX,{"derivedFrom":[subQ1,subQ0]});Q40=makeQuery(id+"F3.imprint","IMPRINT",FACE,{"disambiguationData":[TD([[makeQuery(id+"F3.imprint","IMPRINT",EDGE,{"disambiguationData":[TD([[subQ2,-1.0]])],"derivedFrom":subQ1}),-1.0]])]});}
            var Q41;
            {var subQ0=sQuery(id+"F3.wireOp",EDGE,"E74.trimOffspring");var subQ1=sQuery(id+"F3.wireOp",EDGE,"E69.trimOffspring");var subQ2=makeQuery(id+"F3.imprint","INTERSECT",VERTEX,{"derivedFrom":[subQ1,subQ0]});Q41=makeQuery(id+"F3.imprint","IMPRINT",FACE,{"disambiguationData":[TD([[makeQuery(id+"F3.imprint","IMPRINT",EDGE,{"disambiguationData":[TD([[subQ2,1.0]])],"derivedFrom":subQ1}),-1.0]])]});}
            var Q42;
            Q42=makeQuery(id+"F3.imprint","IMPRINT",FACE,{"disambiguationData":[TD([[makeQuery(id+"F3.imprint","IMPRINT",EDGE,{"derivedFrom":makeQuery(id+"F1.opExtrude","CAP_EDGE",EDGE,{"disambiguationData":[OSD([sQuery(id+"F0.wireOp",EDGE,"E11.2.0.0")])],"isStart":false})}),-1.0]])]});
            var Q43;
            {var subQ0=sQuery(id+"F3.wireOp",EDGE,"E83.trimOffspring");var subQ1=sQuery(id+"F3.wireOp",EDGE,"E73.trimOffspring");var subQ2=makeQuery(id+"F3.imprint","INTERSECT",VERTEX,{"derivedFrom":[subQ1,subQ0]});Q43=makeQuery(id+"F3.imprint","IMPRINT",FACE,{"disambiguationData":[TD([[makeQuery(id+"F3.imprint","IMPRINT",EDGE,{"disambiguationData":[TD([[subQ2,-1.0]])],"derivedFrom":subQ1}),1.0]])]});}
            var Q44;
            {var subQ0=sQuery(id+"F3.wireOp",EDGE,"E83.trimOffspring");var subQ1=sQuery(id+"F3.wireOp",EDGE,"E71.trimOffspring");var subQ2=makeQuery(id+"F3.imprint","INTERSECT",VERTEX,{"derivedFrom":[subQ1,subQ0]});Q44=makeQuery(id+"F3.imprint","IMPRINT",FACE,{"disambiguationData":[TD([[makeQuery(id+"F3.imprint","IMPRINT",EDGE,{"disambiguationData":[TD([[subQ2,-1.0]])],"derivedFrom":subQ1}),-1.0]])]});}
            var Q45;
            {var subQ0=sQuery(id+"F3.wireOp",EDGE,"E72.trimOffspring");var subQ1=sQuery(id+"F3.wireOp",EDGE,"E70.trimOffspring");var subQ2=makeQuery(id+"F3.imprint","INTERSECT",VERTEX,{"derivedFrom":[subQ1,subQ0]});Q45=makeQuery(id+"F3.imprint","IMPRINT",FACE,{"disambiguationData":[TD([[makeQuery(id+"F3.imprint","IMPRINT",EDGE,{"disambiguationData":[TD([[subQ2,-1.0]])],"derivedFrom":subQ1}),-1.0]])]});}
            var Q46;
            {var subQ1=sQuery(id+"F3.wireOp",EDGE,"E24.5");Q46=makeQuery(id+"F3.imprint","IMPRINT",FACE,{"disambiguationData":[TD([[makeQuery(id+"F3.imprint","IMPRINT",EDGE,{"derivedFrom":subQ1}),1.0]])]});}
            var Q47;
            Q47=makeQuery(id+"F3.imprint","IMPRINT",FACE,{"disambiguationData":[TD([[makeQuery(id+"F3.imprint","IMPRINT",EDGE,{"derivedFrom":makeQuery(id+"F1.opExtrude","CAP_EDGE",EDGE,{"disambiguationData":[OSD([sQuery(id+"F0.wireOp",EDGE,"E21.MirrorC")])],"isStart":false})}),1.0]])]});
            var Q48;
            {var subQ0=sQuery(id+"F3.wireOp",EDGE,"E64.trimOffspring");var subQ1=sQuery(id+"F3.wireOp",EDGE,"E58.trimOffspring");var subQ2=makeQuery(id+"F3.imprint","INTERSECT",VERTEX,{"derivedFrom":[subQ1,subQ0]});Q48=makeQuery(id+"F3.imprint","IMPRINT",FACE,{"disambiguationData":[TD([[makeQuery(id+"F3.imprint","IMPRINT",EDGE,{"disambiguationData":[TD([[subQ2,1.0]])],"derivedFrom":subQ1}),1.0]])]});}
            var Q49;
            {var subQ0=sQuery(id+"F3.wireOp",EDGE,"E63.trimOffspring");var subQ1=sQuery(id+"F3.wireOp",EDGE,"E58.trimOffspring");var subQ2=makeQuery(id+"F3.imprint","INTERSECT",VERTEX,{"derivedFrom":[subQ1,subQ0]});Q49=makeQuery(id+"F3.imprint","IMPRINT",FACE,{"disambiguationData":[TD([[makeQuery(id+"F3.imprint","IMPRINT",EDGE,{"disambiguationData":[TD([[subQ2,-1.0]])],"derivedFrom":subQ1}),1.0]])]});}
            var Q50;
            {var subQ0=sQuery(id+"F3.wireOp",EDGE,"E65.trimOffspring");var subQ1=sQuery(id+"F3.wireOp",EDGE,"E57.trimOffspring");var subQ2=makeQuery(id+"F3.imprint","INTERSECT",VERTEX,{"derivedFrom":[subQ1,subQ0]});Q50=makeQuery(id+"F3.imprint","IMPRINT",FACE,{"disambiguationData":[TD([[makeQuery(id+"F3.imprint","IMPRINT",EDGE,{"disambiguationData":[TD([[subQ2,1.0]])],"derivedFrom":subQ1}),-1.0]])]});}
            var Q51;
            {var subQ0=sQuery(id+"F3.wireOp",EDGE,"E65.trimOffspring");var subQ1=sQuery(id+"F3.wireOp",EDGE,"E56.trimOffspring");var subQ2=makeQuery(id+"F3.imprint","INTERSECT",VERTEX,{"derivedFrom":[subQ1,subQ0]});Q51=makeQuery(id+"F3.imprint","IMPRINT",FACE,{"disambiguationData":[TD([[makeQuery(id+"F3.imprint","IMPRINT",EDGE,{"disambiguationData":[TD([[subQ2,1.0]])],"derivedFrom":subQ1}),1.0]])]});}
            var Q52;
            Q52=makeQuery(id+"F3.imprint","IMPRINT",FACE,{"disambiguationData":[TD([[makeQuery(id+"F3.imprint","IMPRINT",EDGE,{"derivedFrom":makeQuery(id+"F1.opExtrude","CAP_EDGE",EDGE,{"disambiguationData":[OSD([sQuery(id+"F0.wireOp",EDGE,"E8.2.0.0")])],"isStart":false})}),-1.0]])]});
            var Q53;
            {var subQ0=sQuery(id+"F3.wireOp",EDGE,"E81.trimOffspring");var subQ1=sQuery(id+"F3.wireOp",EDGE,"E56.trimOffspring");var subQ2=makeQuery(id+"F3.imprint","INTERSECT",VERTEX,{"derivedFrom":[subQ1,subQ0]});Q53=makeQuery(id+"F3.imprint","IMPRINT",FACE,{"disambiguationData":[TD([[makeQuery(id+"F3.imprint","IMPRINT",EDGE,{"disambiguationData":[TD([[subQ2,-1.0]])],"derivedFrom":subQ1}),1.0]])]});}
            var Q54;
            {var subQ0=sQuery(id+"F3.wireOp",EDGE,"E81.trimOffspring");var subQ1=sQuery(id+"F3.wireOp",EDGE,"E57.trimOffspring");var subQ2=makeQuery(id+"F3.imprint","INTERSECT",VERTEX,{"derivedFrom":[subQ1,subQ0]});Q54=makeQuery(id+"F3.imprint","IMPRINT",FACE,{"disambiguationData":[TD([[makeQuery(id+"F3.imprint","IMPRINT",EDGE,{"disambiguationData":[TD([[subQ2,-1.0]])],"derivedFrom":subQ1}),-1.0]])]});}
            var Q55;
            {var subQ0=sQuery(id+"F3.wireOp",EDGE,"E66.trimOffspring");var subQ1=sQuery(id+"F3.wireOp",EDGE,"E55.trimOffspring");var subQ2=makeQuery(id+"F3.imprint","INTERSECT",VERTEX,{"derivedFrom":[subQ1,subQ0]});Q55=makeQuery(id+"F3.imprint","IMPRINT",FACE,{"disambiguationData":[TD([[makeQuery(id+"F3.imprint","IMPRINT",EDGE,{"disambiguationData":[TD([[subQ2,1.0]])],"derivedFrom":subQ1}),-1.0]])]});}
            var Q56;
            {var subQ0=sQuery(id+"F3.wireOp",EDGE,"E66.trimOffspring");var subQ1=sQuery(id+"F3.wireOp",EDGE,"E54.trimOffspring");var subQ2=makeQuery(id+"F3.imprint","INTERSECT",VERTEX,{"derivedFrom":[subQ1,subQ0]});Q56=makeQuery(id+"F3.imprint","IMPRINT",FACE,{"disambiguationData":[TD([[makeQuery(id+"F3.imprint","IMPRINT",EDGE,{"disambiguationData":[TD([[subQ2,1.0]])],"derivedFrom":subQ1}),1.0]])]});}
            var Q57;
            {var subQ0=sQuery(id+"F3.wireOp",EDGE,"E62.trimOffspring");var subQ1=sQuery(id+"F3.wireOp",EDGE,"E54.trimOffspring");var subQ2=makeQuery(id+"F3.imprint","INTERSECT",VERTEX,{"derivedFrom":[subQ1,subQ0]});Q57=makeQuery(id+"F3.imprint","IMPRINT",FACE,{"disambiguationData":[TD([[makeQuery(id+"F3.imprint","IMPRINT",EDGE,{"disambiguationData":[TD([[subQ2,-1.0]])],"derivedFrom":subQ1}),1.0]])]});}
            var Q58;
            {var subQ0=sQuery(id+"F3.wireOp",EDGE,"E62.trimOffspring");var subQ1=sQuery(id+"F3.wireOp",EDGE,"E55.trimOffspring");var subQ2=makeQuery(id+"F3.imprint","INTERSECT",VERTEX,{"derivedFrom":[subQ1,subQ0]});Q58=makeQuery(id+"F3.imprint","IMPRINT",FACE,{"disambiguationData":[TD([[makeQuery(id+"F3.imprint","IMPRINT",EDGE,{"disambiguationData":[TD([[subQ2,-1.0]])],"derivedFrom":subQ1}),-1.0]])]});}
            var Q59;
            Q59=makeQuery(id+"F3.imprint","IMPRINT",FACE,{"disambiguationData":[TD([[makeQuery(id+"F3.imprint","IMPRINT",EDGE,{"derivedFrom":makeQuery(id+"F1.opExtrude","CAP_EDGE",EDGE,{"disambiguationData":[OSD([sQuery(id+"F0.wireOp",EDGE,"E8.1.0.0")])],"isStart":false})}),-1.0]])]});
            var Q60;
            Q60=makeQuery(id+"F3.imprint","IMPRINT",FACE,{"disambiguationData":[TD([[makeQuery(id+"F3.imprint","IMPRINT",EDGE,{"derivedFrom":makeQuery(id+"F1.opExtrude","CAP_EDGE",EDGE,{"disambiguationData":[OSD([sQuery(id+"F0.wireOp",EDGE,"E7")])],"isStart":false})}),-1.0]])]});
            var Q61;
            {var subQ0=sQuery(id+"F3.wireOp",EDGE,"E52.trimOffspring");var subQ1=sQuery(id+"F3.wireOp",EDGE,"E50.trimOffspring");var subQ2=makeQuery(id+"F3.imprint","INTERSECT",VERTEX,{"derivedFrom":[subQ1,subQ0]});Q61=makeQuery(id+"F3.imprint","IMPRINT",FACE,{"disambiguationData":[TD([[makeQuery(id+"F3.imprint","IMPRINT",EDGE,{"disambiguationData":[TD([[subQ2,-1.0]])],"derivedFrom":subQ1}),-1.0]])]});}
            var Q62;
            {var subQ0=sQuery(id+"F3.wireOp",EDGE,"E78");Q62=makeQuery(id+"F3.imprint","IMPRINT",FACE,{"disambiguationData":[TD([[makeQuery(id+"F3.imprint","IMPRINT",EDGE,{"derivedFrom":subQ0}),-1.0]])]});}
            var Q63;
            {var subQ0=sQuery(id+"F3.wireOp",EDGE,"E67.trimOffspring");var subQ1=sQuery(id+"F3.wireOp",EDGE,"E53.trimOffspring");var subQ2=makeQuery(id+"F3.imprint","INTERSECT",VERTEX,{"derivedFrom":[subQ1,subQ0]});Q63=makeQuery(id+"F3.imprint","IMPRINT",FACE,{"disambiguationData":[TD([[makeQuery(id+"F3.imprint","IMPRINT",EDGE,{"disambiguationData":[TD([[subQ2,1.0]])],"derivedFrom":subQ1}),-1.0]])]});}
            var Q64;
            {var subQ0=sQuery(id+"F3.wireOp",EDGE,"E67.trimOffspring");var subQ1=sQuery(id+"F3.wireOp",EDGE,"E52.trimOffspring");var subQ2=makeQuery(id+"F3.imprint","INTERSECT",VERTEX,{"derivedFrom":[subQ1,subQ0]});Q64=makeQuery(id+"F3.imprint","IMPRINT",FACE,{"disambiguationData":[TD([[makeQuery(id+"F3.imprint","IMPRINT",EDGE,{"disambiguationData":[TD([[subQ2,1.0]])],"derivedFrom":subQ1}),1.0]])]});}
            var Q65;
            Q65=makeQuery(id+"F3.imprint","IMPRINT",FACE,{"disambiguationData":[TD([[makeQuery(id+"F3.imprint","IMPRINT",EDGE,{"derivedFrom":makeQuery(id+"F1.opExtrude","CAP_EDGE",EDGE,{"disambiguationData":[OSD([sQuery(id+"F0.wireOp",EDGE,"E18")])],"isStart":false})}),-1.0]])]});
            var Q66;
            {var subQ0=sQuery(id+"F3.wireOp",EDGE,"E36.trimOffspring");var subQ1=sQuery(id+"F3.wireOp",EDGE,"E32.0.2.1");var subQ2=makeQuery(id+"F3.imprint","INTERSECT",VERTEX,{"derivedFrom":[subQ1,subQ0]});Q66=makeQuery(id+"F3.imprint","IMPRINT",FACE,{"disambiguationData":[TD([[makeQuery(id+"F3.imprint","IMPRINT",EDGE,{"disambiguationData":[TD([[subQ2,1.0]])],"derivedFrom":subQ1}),-1.0]])]});}
            var Q67;
            {var subQ0=sQuery(id+"F3.wireOp",EDGE,"E36.trimOffspring");var subQ1=sQuery(id+"F3.wireOp",EDGE,"E32.0.1.0");var subQ2=makeQuery(id+"F3.imprint","INTERSECT",VERTEX,{"derivedFrom":[subQ1,subQ0]});Q67=makeQuery(id+"F3.imprint","IMPRINT",FACE,{"disambiguationData":[TD([[makeQuery(id+"F3.imprint","IMPRINT",EDGE,{"disambiguationData":[TD([[subQ2,1.0]])],"derivedFrom":subQ1}),1.0]])]});}
            var Q68;
            {var subQ0=sQuery(id+"F3.wireOp",EDGE,"E31.1.0.0");var subQ1=sQuery(id+"F3.wireOp",EDGE,"E24.0");var subQ2=makeQuery(id+"F3.imprint","INTERSECT",VERTEX,{"derivedFrom":[subQ1,subQ0]});Q68=makeQuery(id+"F3.imprint","IMPRINT",FACE,{"disambiguationData":[TD([[makeQuery(id+"F3.imprint","IMPRINT",EDGE,{"disambiguationData":[TD([[subQ2,1.0]])],"derivedFrom":subQ1}),1.0]])]});}
            var Q69;
            {var subQ3=sQuery(id+"F3.wireOp",EDGE,"E24.11");Q69=makeQuery(id+"F3.imprint","IMPRINT",FACE,{"disambiguationData":[TD([[makeQuery(id+"F3.imprint","IMPRINT",EDGE,{"derivedFrom":subQ3}),-1.0]])]});}
            var Q70;
            {var subQ0=sQuery(id+"F3.wireOp",EDGE,"E29");var subQ1=sQuery(id+"F3.wireOp",EDGE,"E24.2");var subQ2=makeQuery(id+"F3.imprint","INTERSECT",VERTEX,{"derivedFrom":[subQ1,subQ0]});Q70=makeQuery(id+"F3.imprint","IMPRINT",FACE,{"disambiguationData":[TD([[makeQuery(id+"F3.imprint","IMPRINT",EDGE,{"disambiguationData":[TD([[subQ2,-1.0]])],"derivedFrom":subQ1}),-1.0]])]});}
            var Q71;
            {var subQ0=sQuery(id+"F3.wireOp",EDGE,"E31.2.0.0");var subQ1=sQuery(id+"F3.wireOp",EDGE,"E24.0");var subQ2=makeQuery(id+"F3.imprint","INTERSECT",VERTEX,{"derivedFrom":[subQ1,subQ0]});Q71=makeQuery(id+"F3.imprint","IMPRINT",FACE,{"disambiguationData":[TD([[makeQuery(id+"F3.imprint","IMPRINT",EDGE,{"disambiguationData":[TD([[subQ2,1.0]])],"derivedFrom":subQ1}),1.0]])]});}
            var Q72;
            {var subQ0=sQuery(id+"F3.wireOp",EDGE,"E25.right");Q72=makeQuery(id+"F3.imprint","IMPRINT",FACE,{"disambiguationData":[TD([[makeQuery(id+"F3.imprint","IMPRINT",EDGE,{"derivedFrom":subQ0}),1.0]])]});}
            var Q73;
            {var subQ0=sQuery(id+"F3.wireOp",EDGE,"E64.trimOffspring");var subQ1=sQuery(id+"F3.wireOp",EDGE,"E24.6");var subQ2=makeQuery(id+"F3.imprint","INTERSECT",VERTEX,{"derivedFrom":[subQ1,subQ0]});Q73=makeQuery(id+"F3.imprint","IMPRINT",FACE,{"disambiguationData":[TD([[makeQuery(id+"F3.imprint","IMPRINT",EDGE,{"disambiguationData":[TD([[subQ2,1.0]])],"derivedFrom":subQ1}),1.0]])]});}
            var Q74;
            {var subQ0=sQuery(id+"F3.wireOp",EDGE,"E71.trimOffspring");var subQ1=sQuery(id+"F3.wireOp",EDGE,"E24.4");var subQ2=makeQuery(id+"F3.imprint","INTERSECT",VERTEX,{"derivedFrom":[subQ1,subQ0]});Q74=makeQuery(id+"F3.imprint","IMPRINT",FACE,{"disambiguationData":[TD([[makeQuery(id+"F3.imprint","IMPRINT",EDGE,{"disambiguationData":[TD([[subQ2,1.0]])],"derivedFrom":subQ1}),-1.0]])]});}
            var Q75;
            {var subQ0=sQuery(id+"F3.wireOp",EDGE,"E73.trimOffspring");var subQ1=sQuery(id+"F3.wireOp",EDGE,"E24.4");var subQ2=makeQuery(id+"F3.imprint","INTERSECT",VERTEX,{"derivedFrom":[subQ1,subQ0]});Q75=makeQuery(id+"F3.imprint","IMPRINT",FACE,{"disambiguationData":[TD([[makeQuery(id+"F3.imprint","IMPRINT",EDGE,{"disambiguationData":[TD([[subQ2,-1.0]])],"derivedFrom":subQ1}),-1.0]])]});}
            var Q76;
            {var subQ0=sQuery(id+"F3.wireOp",EDGE,"E75.trimOffspring");var subQ1=sQuery(id+"F3.wireOp",EDGE,"E24.4");var subQ2=makeQuery(id+"F3.imprint","INTERSECT",VERTEX,{"derivedFrom":[subQ1,subQ0]});Q76=makeQuery(id+"F3.imprint","IMPRINT",FACE,{"disambiguationData":[TD([[makeQuery(id+"F3.imprint","IMPRINT",EDGE,{"disambiguationData":[TD([[subQ2,-1.0]])],"derivedFrom":subQ1}),-1.0]])]});}
            var Q77;
            {var subQ0=sQuery(id+"F3.wireOp",EDGE,"E76.trimOffspring");var subQ1=sQuery(id+"F3.wireOp",EDGE,"E24.4");var subQ2=makeQuery(id+"F3.imprint","INTERSECT",VERTEX,{"derivedFrom":[subQ1,subQ0]});Q77=makeQuery(id+"F3.imprint","IMPRINT",FACE,{"disambiguationData":[TD([[makeQuery(id+"F3.imprint","IMPRINT",EDGE,{"disambiguationData":[TD([[subQ2,-1.0]])],"derivedFrom":subQ1}),-1.0]])]});}
            var Q78;
            {var subQ5=sQuery(id+"F3.wireOp",EDGE,"E85.trimOffspring");Q78=makeQuery(id+"F3.imprint","IMPRINT",FACE,{"disambiguationData":[TD([[makeQuery(id+"F3.imprint","IMPRINT",EDGE,{"derivedFrom":subQ5}),-1.0]])]});}
            var Q79;
            {var subQ0=sQuery(id+"F3.wireOp",EDGE,"E49.trimOffspring");var subQ1=sQuery(id+"F3.wireOp",EDGE,"E24.12");var subQ2=makeQuery(id+"F3.imprint","INTERSECT",VERTEX,{"derivedFrom":[subQ1,subQ0]});Q79=makeQuery(id+"F3.imprint","IMPRINT",FACE,{"disambiguationData":[TD([[makeQuery(id+"F3.imprint","IMPRINT",EDGE,{"disambiguationData":[TD([[subQ2,1.0]])],"derivedFrom":subQ1}),-1.0]])]});}
            var Q80;
            {var subQ3=sQuery(id+"F3.wireOp",EDGE,"E67.trimOffspring");var subQ5=sQuery(id+"F3.wireOp",EDGE,"E24.19");var subQ6=makeQuery(id+"F3.imprint","INTERSECT",VERTEX,{"derivedFrom":[subQ5,subQ3]});Q80=makeQuery(id+"F3.imprint","IMPRINT",FACE,{"disambiguationData":[TD([[makeQuery(id+"F3.imprint","IMPRINT",EDGE,{"disambiguationData":[TD([[subQ6,1.0]])],"derivedFrom":subQ5}),-1.0]])]});}
            var Q81;
            {var subQ0=sQuery(id+"F3.wireOp",EDGE,"E65.trimOffspring");var subQ1=sQuery(id+"F3.wireOp",EDGE,"E24.16");var subQ2=makeQuery(id+"F3.imprint","INTERSECT",VERTEX,{"derivedFrom":[subQ1,subQ0]});Q81=makeQuery(id+"F3.imprint","IMPRINT",FACE,{"disambiguationData":[TD([[makeQuery(id+"F3.imprint","IMPRINT",EDGE,{"disambiguationData":[TD([[subQ2,-1.0]])],"derivedFrom":subQ1}),-1.0]])]});}
            var Q82;
            {var subQ0=sQuery(id+"F3.wireOp",EDGE,"E60.trimOffspring");var subQ1=sQuery(id+"F3.wireOp",EDGE,"E24.14");var subQ2=makeQuery(id+"F3.imprint","INTERSECT",VERTEX,{"derivedFrom":[subQ1,subQ0]});Q82=makeQuery(id+"F3.imprint","IMPRINT",FACE,{"disambiguationData":[TD([[makeQuery(id+"F3.imprint","IMPRINT",EDGE,{"disambiguationData":[TD([[subQ2,1.0]])],"derivedFrom":subQ1}),-1.0]])]});}
            var Q83;
            {var subQ0=sQuery(id+"F3.wireOp",EDGE,"E44.trimOffspring");var subQ1=sQuery(id+"F3.wireOp",EDGE,"E24.8");var subQ2=makeQuery(id+"F3.imprint","INTERSECT",VERTEX,{"derivedFrom":[subQ1,subQ0]});Q83=makeQuery(id+"F3.imprint","IMPRINT",FACE,{"disambiguationData":[TD([[makeQuery(id+"F3.imprint","IMPRINT",EDGE,{"disambiguationData":[TD([[subQ2,-1.0]])],"derivedFrom":subQ1}),-1.0]])]});}
            var Q84;
            {var subQ5=sQuery(id+"F3.wireOp",EDGE,"E84.trimOffspring");Q84=makeQuery(id+"F3.imprint","IMPRINT",FACE,{"disambiguationData":[TD([[makeQuery(id+"F3.imprint","IMPRINT",EDGE,{"derivedFrom":subQ5}),-1.0]])]});}
            var Q85;
            {var subQ0=sQuery(id+"F3.wireOp",EDGE,"E31.3.0.0");var subQ1=sQuery(id+"F3.wireOp",EDGE,"E24.0");var subQ2=makeQuery(id+"F3.imprint","INTERSECT",VERTEX,{"derivedFrom":[subQ1,subQ0]});Q85=makeQuery(id+"F3.imprint","IMPRINT",FACE,{"disambiguationData":[TD([[makeQuery(id+"F3.imprint","IMPRINT",EDGE,{"disambiguationData":[TD([[subQ2,1.0]])],"derivedFrom":subQ1}),1.0]])]});}
            extrude(context, id + "F4", {"entities" : qUnion([Q0, Q1, Q2, Q3, Q4, Q5, Q6, Q7, Q8, Q9, Q10, Q11, Q12, Q13, Q14, Q15, Q16, Q17, Q18, Q19, Q20, Q21, Q22, Q23, Q24, Q25, Q26, Q27, Q28, Q29, Q30, Q31, Q32, Q33, Q34, Q35, Q36, Q37, Q38, Q39, Q40, Q41, Q42, Q43, Q44, Q45, Q46, Q47, Q48, Q49, Q50, Q51, Q52, Q53, Q54, Q55, Q56, Q57, Q58, Q59, Q60, Q61, Q62, Q63, Q64, Q65, Q66, Q67, Q68, Q69, Q70, Q71, Q72, Q73, Q74, Q75, Q76, Q77, Q78, Q79, Q80, Q81, Q82, Q83, Q84, Q85]), "operationType" : NewBodyOperationType.ADD, "depth" : 2 * mm});
        }
        {
            var Q0;
            Q0=makeQuery(id+"F4.opExtrude","SWEPT_EDGE",EDGE,{"disambiguationData":[OSD([sQuery(id+"F3.wireOp",EDGE,"E27"),sQuery(id+"F3.wireOp",EDGE,"E32.0.2.0")])]});
            var Q1;
            Q1=makeQuery(id+"F4.opExtrude","SWEPT_EDGE",EDGE,{"disambiguationData":[OSD([sQuery(id+"F3.wireOp",EDGE,"E28.MirrorCS"),sQuery(id+"F3.wireOp",EDGE,"E34.trimOffspring")])]});
            var Q2;
            Q2=makeQuery(id+"F4.opExtrude","SWEPT_EDGE",EDGE,{"disambiguationData":[OSD([sQuery(id+"F3.wireOp",EDGE,"E31.1.0.0"),sQuery(id+"F3.wireOp",EDGE,"E34.trimOffspring")])]});
            var Q3;
            Q3=makeQuery(id+"F4.opExtrude","SWEPT_EDGE",EDGE,{"disambiguationData":[OSD([sQuery(id+"F3.wireOp",EDGE,"E31.1.0.1"),sQuery(id+"F3.wireOp",EDGE,"E43.trimOffspring")])]});
            var Q4;
            Q4=makeQuery(id+"F4.opExtrude","SWEPT_EDGE",EDGE,{"disambiguationData":[OSD([sQuery(id+"F3.wireOp",EDGE,"E31.2.0.0"),sQuery(id+"F3.wireOp",EDGE,"E43.trimOffspring")])]});
            var Q5;
            Q5=makeQuery(id+"F4.opExtrude","SWEPT_EDGE",EDGE,{"disambiguationData":[OSD([sQuery(id+"F3.wireOp",EDGE,"E31.2.0.1"),sQuery(id+"F3.wireOp",EDGE,"E44.trimOffspring")])]});
            var Q6;
            Q6=makeQuery(id+"F4.opExtrude","SWEPT_EDGE",EDGE,{"disambiguationData":[OSD([sQuery(id+"F3.wireOp",EDGE,"E31.3.0.0"),sQuery(id+"F3.wireOp",EDGE,"E44.trimOffspring")])]});
            var Q7;
            Q7=makeQuery(id+"F4.opExtrude","SWEPT_EDGE",EDGE,{"disambiguationData":[OSD([sQuery(id+"F3.wireOp",EDGE,"E31.3.0.1"),sQuery(id+"F3.wireOp",EDGE,"E45.trimOffspring")])]});
            var Q8;
            Q8=makeQuery(id+"F4.opExtrude","SWEPT_EDGE",EDGE,{"disambiguationData":[OSD([sQuery(id+"F3.wireOp",EDGE,"E42.trimOffspring"),sQuery(id+"F3.wireOp",EDGE,"E61.trimOffspring")])]});
            var Q9;
            Q9=makeQuery(id+"F4.opExtrude","SWEPT_EDGE",EDGE,{"disambiguationData":[OSD([sQuery(id+"F3.wireOp",EDGE,"E41.trimOffspring"),sQuery(id+"F3.wireOp",EDGE,"E60.trimOffspring")])]});
            var Q10;
            Q10=makeQuery(id+"F4.opExtrude","SWEPT_EDGE",EDGE,{"disambiguationData":[OSD([sQuery(id+"F3.wireOp",EDGE,"E40.trimOffspring"),sQuery(id+"F3.wireOp",EDGE,"E60.trimOffspring")])]});
            var Q11;
            Q11=makeQuery(id+"F4.opExtrude","SWEPT_EDGE",EDGE,{"disambiguationData":[OSD([sQuery(id+"F3.wireOp",EDGE,"E39.trimOffspring"),sQuery(id+"F3.wireOp",EDGE,"E59.trimOffspring")])]});
            var Q12;
            Q12=makeQuery(id+"F4.opExtrude","SWEPT_EDGE",EDGE,{"disambiguationData":[OSD([sQuery(id+"F3.wireOp",EDGE,"E37.trimOffspring"),sQuery(id+"F3.wireOp",EDGE,"E49.trimOffspring")])]});
            var Q13;
            Q13=makeQuery(id+"F4.opExtrude","SWEPT_EDGE",EDGE,{"disambiguationData":[OSD([sQuery(id+"F3.wireOp",EDGE,"E38.trimOffspring"),sQuery(id+"F3.wireOp",EDGE,"E59.trimOffspring")])]});
            var Q14;
            Q14=makeQuery(id+"F4.opExtrude","SWEPT_EDGE",EDGE,{"disambiguationData":[OSD([sQuery(id+"F3.wireOp",EDGE,"E32.0.1.0"),sQuery(id+"F3.wireOp",EDGE,"E36.trimOffspring")])]});
            var Q15;
            Q15=makeQuery(id+"F4.opExtrude","SWEPT_EDGE",EDGE,{"disambiguationData":[OSD([sQuery(id+"F3.wireOp",EDGE,"E35.trimOffspring"),sQuery(id+"F3.wireOp",EDGE,"E49.trimOffspring")])]});
            var Q16;
            Q16=makeQuery(id+"F4.opExtrude","SWEPT_EDGE",EDGE,{"disambiguationData":[OSD([sQuery(id+"F3.wireOp",EDGE,"E32.0.1.1"),sQuery(id+"F3.wireOp",EDGE,"E51.trimOffspring")])]});
            var Q17;
            Q17=makeQuery(id+"F4.opExtrude","SWEPT_EDGE",EDGE,{"disambiguationData":[OSD([sQuery(id+"F3.wireOp",EDGE,"E30.MirrorCS"),sQuery(id+"F3.wireOp",EDGE,"E51.trimOffspring")])]});
            var Q18;
            Q18=makeQuery(id+"F4.opExtrude","SWEPT_EDGE",EDGE,{"disambiguationData":[OSD([sQuery(id+"F3.wireOp",EDGE,"E52.trimOffspring"),sQuery(id+"F3.wireOp",EDGE,"E67.trimOffspring")])]});
            var Q19;
            Q19=makeQuery(id+"F4.opExtrude","SWEPT_EDGE",EDGE,{"disambiguationData":[OSD([sQuery(id+"F3.wireOp",EDGE,"E53.trimOffspring"),sQuery(id+"F3.wireOp",EDGE,"E67.trimOffspring")])]});
            var Q20;
            Q20=makeQuery(id+"F4.opExtrude","SWEPT_EDGE",EDGE,{"disambiguationData":[OSD([sQuery(id+"F3.wireOp",EDGE,"E53.trimOffspring"),sQuery(id+"F3.wireOp",EDGE,"E78")])]});
            var Q21;
            Q21=makeQuery(id+"F4.opExtrude","SWEPT_EDGE",EDGE,{"disambiguationData":[OSD([sQuery(id+"F3.wireOp",EDGE,"E54.trimOffspring"),sQuery(id+"F3.wireOp",EDGE,"E66.trimOffspring")])]});
            var Q22;
            Q22=makeQuery(id+"F4.opExtrude","SWEPT_EDGE",EDGE,{"disambiguationData":[OSD([sQuery(id+"F3.wireOp",EDGE,"E55.trimOffspring"),sQuery(id+"F3.wireOp",EDGE,"E66.trimOffspring")])]});
            var Q23;
            Q23=makeQuery(id+"F4.opExtrude","SWEPT_EDGE",EDGE,{"disambiguationData":[OSD([sQuery(id+"F3.wireOp",EDGE,"E55.trimOffspring"),sQuery(id+"F3.wireOp",EDGE,"E62.trimOffspring")])]});
            var Q24;
            Q24=makeQuery(id+"F4.opExtrude","SWEPT_EDGE",EDGE,{"disambiguationData":[OSD([sQuery(id+"F3.wireOp",EDGE,"E56.trimOffspring"),sQuery(id+"F3.wireOp",EDGE,"E65.trimOffspring")])]});
            var Q25;
            Q25=makeQuery(id+"F4.opExtrude","SWEPT_EDGE",EDGE,{"disambiguationData":[OSD([sQuery(id+"F3.wireOp",EDGE,"E57.trimOffspring"),sQuery(id+"F3.wireOp",EDGE,"E65.trimOffspring")])]});
            var Q26;
            Q26=makeQuery(id+"F4.opExtrude","SWEPT_EDGE",EDGE,{"disambiguationData":[OSD([sQuery(id+"F3.wireOp",EDGE,"E58.trimOffspring"),sQuery(id+"F3.wireOp",EDGE,"E64.trimOffspring")])]});
            var Q27;
            Q27=makeQuery(id+"F4.opExtrude","SWEPT_EDGE",EDGE,{"disambiguationData":[OSD([sQuery(id+"F3.wireOp",EDGE,"E57.trimOffspring"),sQuery(id+"F3.wireOp",EDGE,"E81.trimOffspring")])]});
            var Q28;
            Q28=makeQuery(id+"F4.opExtrude","SWEPT_EDGE",EDGE,{"disambiguationData":[OSD([sQuery(id+"F3.wireOp",EDGE,"E71.trimOffspring"),sQuery(id+"F3.wireOp",EDGE,"E83.trimOffspring")])]});
            var Q29;
            Q29=makeQuery(id+"F4.opExtrude","SWEPT_EDGE",EDGE,{"disambiguationData":[OSD([sQuery(id+"F3.wireOp",EDGE,"E29"),sQuery(id+"F3.wireOp",EDGE,"E77.trimOffspring")])]});
            var Q30;
            Q30=makeQuery(id+"F4.opExtrude","SWEPT_EDGE",EDGE,{"disambiguationData":[OSD([sQuery(id+"F3.wireOp",EDGE,"E68.trimOffspring"),sQuery(id+"F3.wireOp",EDGE,"E76.trimOffspring")])]});
            var Q31;
            Q31=makeQuery(id+"F4.opExtrude","SWEPT_EDGE",EDGE,{"disambiguationData":[OSD([sQuery(id+"F3.wireOp",EDGE,"E79"),sQuery(id+"F3.wireOp",EDGE,"E80.trimOffspring")])]});
            var Q32;
            Q32=makeQuery(id+"F4.opExtrude","SWEPT_EDGE",EDGE,{"disambiguationData":[OSD([sQuery(id+"F3.wireOp",EDGE,"E69.trimOffspring"),sQuery(id+"F3.wireOp",EDGE,"E75.trimOffspring")])]});
            var Q33;
            Q33=makeQuery(id+"F4.opExtrude","SWEPT_EDGE",EDGE,{"disambiguationData":[OSD([sQuery(id+"F3.wireOp",EDGE,"E69.trimOffspring"),sQuery(id+"F3.wireOp",EDGE,"E74.trimOffspring")])]});
            var Q34;
            Q34=makeQuery(id+"F4.opExtrude","SWEPT_EDGE",EDGE,{"disambiguationData":[OSD([sQuery(id+"F3.wireOp",EDGE,"E73.trimOffspring"),sQuery(id+"F3.wireOp",EDGE,"E83.trimOffspring")])]});
            var Q35;
            Q35=makeQuery(id+"F4.opExtrude","SWEPT_EDGE",EDGE,{"disambiguationData":[OSD([sQuery(id+"F3.wireOp",EDGE,"E70.trimOffspring"),sQuery(id+"F3.wireOp",EDGE,"E72.trimOffspring")])]});
            var Q36;
            Q36=makeQuery(id+"F4.opExtrude","SWEPT_EDGE",EDGE,{"disambiguationData":[OSD([sQuery(id+"F3.wireOp",EDGE,"E58.trimOffspring"),sQuery(id+"F3.wireOp",EDGE,"E63.trimOffspring")])]});
            var Q37;
            Q37=makeQuery(id+"F4.opExtrude","SWEPT_EDGE",EDGE,{"disambiguationData":[OSD([sQuery(id+"F3.wireOp",EDGE,"E56.trimOffspring"),sQuery(id+"F3.wireOp",EDGE,"E81.trimOffspring")])]});
            var Q38;
            Q38=makeQuery(id+"F4.opExtrude","SWEPT_EDGE",EDGE,{"disambiguationData":[OSD([sQuery(id+"F3.wireOp",EDGE,"E54.trimOffspring"),sQuery(id+"F3.wireOp",EDGE,"E62.trimOffspring")])]});
            var Q39;
            Q39=makeQuery(id+"F4.opExtrude","SWEPT_EDGE",EDGE,{"disambiguationData":[OSD([sQuery(id+"F3.wireOp",EDGE,"E50.trimOffspring"),sQuery(id+"F3.wireOp",EDGE,"E52.trimOffspring")])]});
            var Q40;
            Q40=makeQuery(id+"F4.opExtrude","SWEPT_EDGE",EDGE,{"disambiguationData":[OSD([sQuery(id+"F3.wireOp",EDGE,"E40.trimOffspring"),sQuery(id+"F3.wireOp",EDGE,"E47.trimOffspring")])]});
            var Q41;
            Q41=makeQuery(id+"F4.opExtrude","SWEPT_EDGE",EDGE,{"disambiguationData":[OSD([sQuery(id+"F3.wireOp",EDGE,"E41.trimOffspring"),sQuery(id+"F3.wireOp",EDGE,"E47.trimOffspring")])]});
            var Q42;
            Q42=makeQuery(id+"F4.opExtrude","SWEPT_EDGE",EDGE,{"disambiguationData":[OSD([sQuery(id+"F3.wireOp",EDGE,"E42.trimOffspring"),sQuery(id+"F3.wireOp",EDGE,"E46.trimOffspring")])]});
            var Q43;
            Q43=makeQuery(id+"F4.opExtrude","SWEPT_EDGE",EDGE,{"disambiguationData":[OSD([sQuery(id+"F3.wireOp",EDGE,"E39.trimOffspring"),sQuery(id+"F3.wireOp",EDGE,"E48.trimOffspring")])]});
            var Q44;
            Q44=makeQuery(id+"F4.opExtrude","SWEPT_EDGE",EDGE,{"disambiguationData":[OSD([sQuery(id+"F3.wireOp",EDGE,"E32.0.2.1"),sQuery(id+"F3.wireOp",EDGE,"E36.trimOffspring")])]});
            var Q45;
            Q45=makeQuery(id+"F4.opExtrude","SWEPT_EDGE",EDGE,{"disambiguationData":[OSD([sQuery(id+"F3.wireOp",EDGE,"E33.trimOffspring"),sQuery(id+"F3.wireOp",EDGE,"E35.trimOffspring")])]});
            var Q46;
            Q46=makeQuery(id+"F4.opExtrude","SWEPT_EDGE",EDGE,{"disambiguationData":[OSD([sQuery(id+"F3.wireOp",EDGE,"E33.trimOffspring"),sQuery(id+"F3.wireOp",EDGE,"E37.trimOffspring")])]});
            var Q47;
            Q47=makeQuery(id+"F4.opExtrude","SWEPT_EDGE",EDGE,{"disambiguationData":[OSD([sQuery(id+"F3.wireOp",EDGE,"E38.trimOffspring"),sQuery(id+"F3.wireOp",EDGE,"E48.trimOffspring")])]});
            fillet(context, id + "F5", {"entities" : qUnion([Q0, Q1, Q2, Q3, Q4, Q5, Q6, Q7, Q8, Q9, Q10, Q11, Q12, Q13, Q14, Q15, Q16, Q17, Q18, Q19, Q20, Q21, Q22, Q23, Q24, Q25, Q26, Q27, Q28, Q29, Q30, Q31, Q32, Q33, Q34, Q35, Q36, Q37, Q38, Q39, Q40, Q41, Q42, Q43, Q44, Q45, Q46, Q47]), "radius" : 1 * mm, "tangentPropagation" : true, "conicFillet" : false});
        }
    });
